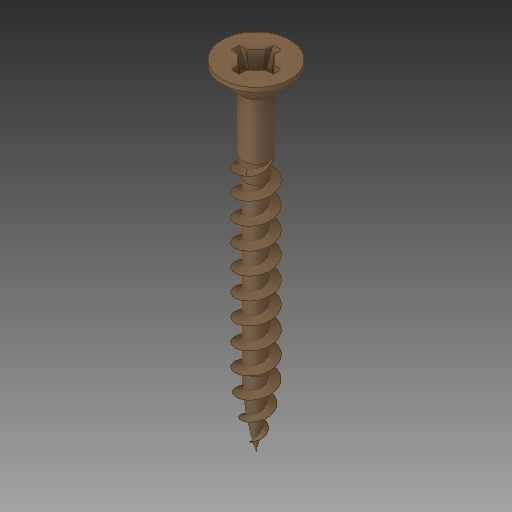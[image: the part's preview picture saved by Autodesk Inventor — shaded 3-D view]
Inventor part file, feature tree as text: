
AUTODESK INVENTOR PART (.ipt)
format: ipt  version: 2018.2 (Build 222227000, 227)  size: 736,768 bytes
history: native  units: in
note: dims shown in document units (in); Inventor stores cm internally (conversion verified against a paired STEP export)
features: other x1, thread x1
ambient origin geometry x8: Origin, YZ Plane, XZ Plane, XY Plane, X Axis, Y Axis, Z Axis, Center Point
bodies: Solid1 (feature_tree), Solid2 (feature_tree)
feature tree (2):
  parser-record x1  (decoder bookkeeping rows leaked as tree rows — omitted from the tree; the rows remain in map.json)
  thread  "Thread-1"  [1 undecoded]
note: 1 required parameter value undecoded (feature->parameter linkage not recoverable at this tier; creation-order binding heuristic only, values carry confidence <= 0.55)
